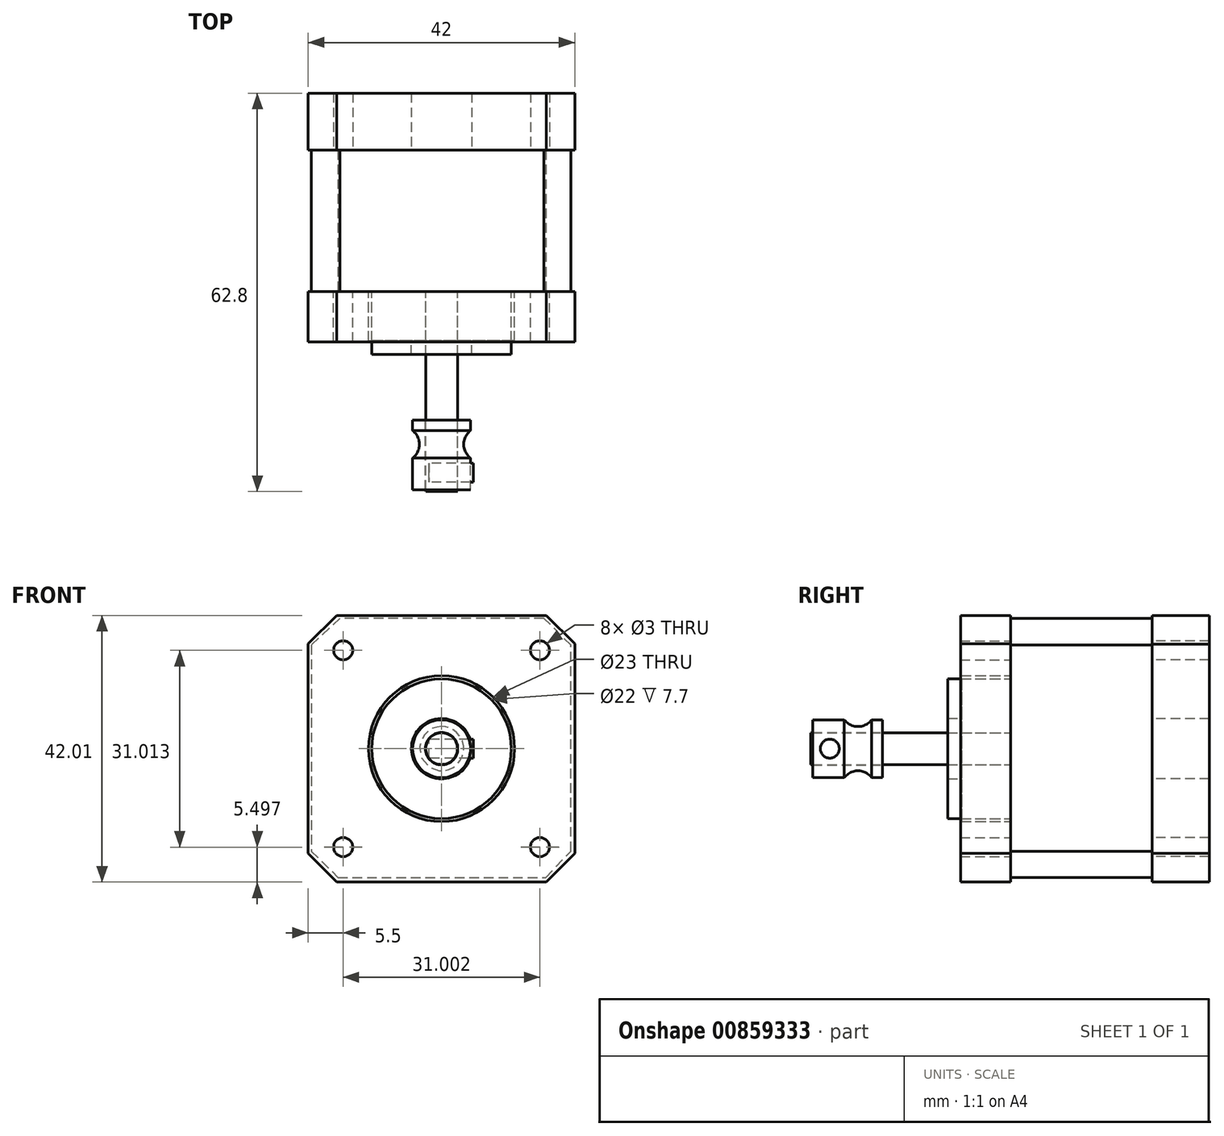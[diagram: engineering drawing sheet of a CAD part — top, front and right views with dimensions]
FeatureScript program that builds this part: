
annotation { "Feature Type Name" : "Feature", "Feature Type Description" : "" }
export const myFeature = defineFeature(function(context is Context, id is Id, definition is map)
    precondition{}
    {
        {
            var Q0;
            Q0=qCreatedBy(makeId("Front.planeOp"),FACE);
            var sketch = newSketch(context, id + "F0", { "sketchPlane" : qUnion([Q0])});
            skLineSegment(sketch, "E0.bottom", {"start": v(-16.5, 21) * mm, "end": v(16.5, 21) * mm});
            skLineSegment(sketch, "E0.top", {"start": v(-16.5, -21) * mm, "end": v(16.5, -21) * mm});
            skLineSegment(sketch, "E0.left", {"start": v(-21, 16.5) * mm, "end": v(-21, -16.5) * mm});
            skLineSegment(sketch, "E0.right", {"start": v(21, 16.5) * mm, "end": v(21, -16.5) * mm});
            skPoint(sketch, "E0.middle", {"position": v(0, 0) * mm});
            skLineSegment(sketch, "E1", {"start": v(-21, 16.5) * mm, "end": v(-16.5, 21) * mm});
            skLineSegment(sketch, "E2.MirrorCS", {"start": v(21, 16.5) * mm, "end": v(16.5, 21) * mm});
            skLineSegment(sketch, "E3.MirrorCS", {"start": v(-21, -16.5) * mm, "end": v(-16.5, -21) * mm});
            skLineSegment(sketch, "E4.MirrorCS", {"start": v(21, -16.5) * mm, "end": v(16.5, -21) * mm});
            skPoint(sketch, "E5.orphan", {"position": v(-21, 21) * mm});
            skPoint(sketch, "E6.orphan", {"position": v(-21, -21) * mm});
            skPoint(sketch, "E7.orphan", {"position": v(21, -21) * mm});
            skPoint(sketch, "E8.orphan", {"position": v(21, 21) * mm});
            skCircle(sketch, "E9", {"center": v(-15.5, 15.5) * mm, "radius": 1.5 * mm});
            skCircle(sketch, "E10.MirrorC", {"center": v(-15.5, -15.5) * mm, "radius": 1.5 * mm});
            skCircle(sketch, "E11.MirrorC", {"center": v(15.5, 15.5) * mm, "radius": 1.5 * mm});
            skCircle(sketch, "E12.MirrorC", {"center": v(15.5, -15.5) * mm, "radius": 1.5 * mm});
            skCircle(sketch, "E13", {"center": v(0, 0) * mm, "radius": 11 * mm});
            skCircle(sketch, "E14", {"center": v(0, 0) * mm, "radius": 2.5 * mm});
            skCircle(sketch, "E15", {"center": v(0, 0) * mm, "radius": 4.75 * mm});
            skCircle(sketch, "E16", {"center": v(0, 0) * mm, "radius": 11.5 * mm});
            skLineSegment(sketch, "E17", {"start": v(0, 0) * mm, "end": v(-109.37, 0) * mm, "construction": true});
            skSolve(sketch);
        }
        {
            var Q0;
            Q0=makeQuery(id+"F0.imprint","IMPRINT",FACE,{"disambiguationData":[TD([[makeQuery(id+"F0.imprint","IMPRINT",EDGE,{"derivedFrom":sQuery(id+"F0.wireOp",EDGE,"E0.bottom")}),-1.0]])]});
            extrude(context, id + "F1", {"entities" : qUnion([Q0]), "depth" : 7.9 * mm, "offsetDistance" : 25 * mm});
        }
        {
            var Q0;
            Q0=makeQuery(id+"F0.imprint","IMPRINT",FACE,{"disambiguationData":[TD([[makeQuery(id+"F0.imprint","IMPRINT",EDGE,{"derivedFrom":sQuery(id+"F0.wireOp",EDGE,"E13")}),1.0]])]});
            extrude(context, id + "F2", {"entities" : qUnion([Q0]), "operationType" : NewBodyOperationType.ADD, "depth" : 9.9 * mm, "offsetDistance" : 25 * mm});
        }
        {
            var Q0;
            Q0=makeQuery(id+"F0.imprint","IMPRINT",FACE,{"disambiguationData":[TD([[makeQuery(id+"F0.imprint","IMPRINT",EDGE,{"derivedFrom":sQuery(id+"F0.wireOp",EDGE,"E14")}),-1.0]])]});
            extrude(context, id + "F3", {"entities" : qUnion([Q0]), "operationType" : NewBodyOperationType.ADD, "depth" : 7.9 * mm, "offsetDistance" : 25 * mm});
        }
        {
            var Q0;
            Q0=makeQuery(id+"F0.imprint","IMPRINT",FACE,{"disambiguationData":[TD([[makeQuery(id+"F0.imprint","IMPRINT",EDGE,{"derivedFrom":sQuery(id+"F0.wireOp",EDGE,"E14")}),1.0]])]});
            var Q1;
            Q1=qSketchRegion(id+"F6",true);
            extrude(context, id + "F4", {"entities" : qUnion([Q0, Q1]), "depth" : 31.5 * mm, "offsetDistance" : 25 * mm});
        }
        {
            var Q0;
            Q0=makeQuery(id+"F0.imprint","IMPRINT",FACE,{"disambiguationData":[TD([[makeQuery(id+"F0.imprint","IMPRINT",EDGE,{"derivedFrom":sQuery(id+"F0.wireOp",EDGE,"E13")}),-1.0]])]});
            extrude(context, id + "F5", {"entities" : qUnion([Q0]), "depth" : 7.7 * mm, "offsetDistance" : 25 * mm});
        }
        {
            var Q0;
            Q0=qCreatedBy(makeId("Front.planeOp"),FACE);
            var sketch = newSketch(context, id + "F6", { "sketchPlane" : qUnion([Q0])});
            skLineSegment(sketch, "E18", {"start": v(16.13, 20.56) * mm, "end": v(-16.02, 20.56) * mm});
            skLineSegment(sketch, "E19", {"start": v(-16.02, 20.56) * mm, "end": v(-20.52, 16.32) * mm});
            skLineSegment(sketch, "E20", {"start": v(-20.52, 16.32) * mm, "end": v(-20.52, -16.15) * mm});
            skLineSegment(sketch, "E21", {"start": v(-20.52, -16.15) * mm, "end": v(-16.32, -20.27) * mm});
            skLineSegment(sketch, "E22", {"start": v(-16.32, -20.27) * mm, "end": v(16.41, -20.27) * mm});
            skLineSegment(sketch, "E23", {"start": v(16.41, -20.27) * mm, "end": v(20.38, -16.15) * mm});
            skLineSegment(sketch, "E24", {"start": v(20.38, -16.15) * mm, "end": v(20.38, 16.32) * mm});
            skLineSegment(sketch, "E25", {"start": v(20.38, 16.32) * mm, "end": v(16.13, 20.56) * mm});
            skSolve(sketch);
        }
        {
            var Q0;
            Q0=makeQuery(id+"F6.imprint","IMPRINT",FACE,{"disambiguationData":[TD([[makeQuery(id+"F6.imprint","IMPRINT",EDGE,{"derivedFrom":sQuery(id+"F6.wireOp",EDGE,"E18")}),1.0]])]});
            extrude(context, id + "F7", {"entities" : qUnion([Q0]), "depth" : -22.3 * mm, "offsetDistance" : 25 * mm});
        }
        {
            var Q0;
            Q0=makeQuery(id+"F7.opExtrude","CAP_FACE",FACE,{"disambiguationData":[OSD([sQuery(id+"F6.wireOp",EDGE,"E18"),sQuery(id+"F6.wireOp",EDGE,"E19"),sQuery(id+"F6.wireOp",EDGE,"E20"),sQuery(id+"F6.wireOp",EDGE,"E21"),sQuery(id+"F6.wireOp",EDGE,"E22"),sQuery(id+"F6.wireOp",EDGE,"E23"),sQuery(id+"F6.wireOp",EDGE,"E24"),sQuery(id+"F6.wireOp",EDGE,"E25")])],"isStart":false});
            var sketch = newSketch(context, id + "F8", { "sketchPlane" : qUnion([Q0])});
            skLineSegment(sketch, "E26.bottom", {"start": v(-16.5, 20.99) * mm, "end": v(16.5, 20.99) * mm});
            skLineSegment(sketch, "E26.top", {"start": v(-16.5, -21.01) * mm, "end": v(16.5, -21.01) * mm});
            skLineSegment(sketch, "E26.left", {"start": v(-21, 16.49) * mm, "end": v(-21, -16.51) * mm});
            skLineSegment(sketch, "E26.right", {"start": v(21, 16.49) * mm, "end": v(21, -16.51) * mm});
            skPoint(sketch, "E26.middle", {"position": v(0, -0.01) * mm});
            skLineSegment(sketch, "E27", {"start": v(-21, 16.49) * mm, "end": v(-16.5, 20.99) * mm});
            skLineSegment(sketch, "E28.MirrorCS", {"start": v(21, 16.49) * mm, "end": v(16.5, 20.99) * mm});
            skLineSegment(sketch, "E29.MirrorCS", {"start": v(-21, -16.51) * mm, "end": v(-16.5, -21.01) * mm});
            skLineSegment(sketch, "E30.MirrorCS", {"start": v(21, -16.51) * mm, "end": v(16.5, -21.01) * mm});
            skPoint(sketch, "E31.orphan", {"position": v(-21, 20.99) * mm});
            skPoint(sketch, "E32.orphan", {"position": v(-21, -21.01) * mm});
            skPoint(sketch, "E33.orphan", {"position": v(21, -21.01) * mm});
            skPoint(sketch, "E34.orphan", {"position": v(21, 20.99) * mm});
            skCircle(sketch, "E35", {"center": v(-15.5, 15.49) * mm, "radius": 1.5 * mm});
            skCircle(sketch, "E36.MirrorC", {"center": v(-15.5, -15.51) * mm, "radius": 1.5 * mm});
            skCircle(sketch, "E37.MirrorC", {"center": v(15.5, 15.49) * mm, "radius": 1.5 * mm});
            skCircle(sketch, "E38.MirrorC", {"center": v(15.5, -15.51) * mm, "radius": 1.5 * mm});
            skCircle(sketch, "E39", {"center": v(0, -0.01) * mm, "radius": 2.5 * mm});
            skCircle(sketch, "E40", {"center": v(0, -0.01) * mm, "radius": 4.75 * mm});
            skSolve(sketch);
        }
        {
            var Q0;
            Q0=qSketchRegion(id+"F8",true);
            extrude(context, id + "F9", {"entities" : qUnion([Q0]), "depth" : 9 * mm, "offsetDistance" : 25 * mm});
        }
        {
            var Q0;
            Q0=qCreatedBy(makeId("Right.planeOp"),FACE);
            var sketch = newSketch(context, id + "F10", { "sketchPlane" : qUnion([Q0])});
            skLineSegment(sketch, "E41", {"start": v(-31.2, 2.56) * mm, "end": v(-31.2, 4.56) * mm});
            skLineSegment(sketch, "E42", {"start": v(-31.2, 4.56) * mm, "end": v(-26.2, 4.56) * mm});
            skArc(sketch, "E43", {"start": v(-26.2, 4.56) * mm, "mid": v(-24.05, 3.48) * mm, "end": v(-21.9, 4.56) * mm});
            skLineSegment(sketch, "E44", {"start": v(-21.9, 4.56) * mm, "end": v(-20.2, 4.56) * mm});
            skLineSegment(sketch, "E45", {"start": v(-20.2, 4.56) * mm, "end": v(-20.2, 2.56) * mm});
            skLineSegment(sketch, "E46", {"start": v(-20.2, 2.56) * mm, "end": v(-31.2, 2.56) * mm});
            skLineSegment(sketch, "E47", {"start": v(0, 0) * mm, "end": v(-43.23, 0) * mm, "construction": true});
            skLineSegment(sketch, "E48", {"start": v(-24.05, 6.17) * mm, "end": v(-24.05, 14.68) * mm, "construction": true});
            skSolve(sketch);
        }
        {
            var Q0;
            Q0=makeQuery(id+"F10.imprint","IMPRINT",FACE,{"disambiguationData":[TD([[makeQuery(id+"F10.imprint","IMPRINT",EDGE,{"derivedFrom":sQuery(id+"F10.wireOp",EDGE,"E41")}),-1.0]])]});
            var Q1;
            Q1=sQuery(id+"F10.wireOp",EDGE,"E47");
            revolve(context, id + "F11", {"surfaceOperationType" : NewSurfaceOperationType.NEW, "entities" : qUnion([Q0]), "axis" : qUnion([Q1]), "revolveType" : RevolveType.FULL});
        }
        {
            var Q0;
            Q0=qCreatedBy(makeId("Right.planeOp"),FACE);
            var sketch = newSketch(context, id + "F12", { "sketchPlane" : qUnion([Q0])});
            skPoint(sketch, "E49", {"position": v(-28.5, 0) * mm});
            skCircle(sketch, "E50", {"center": v(-28.5, 0) * mm, "radius": 1.5 * mm});
            skSolve(sketch);
        }
        {
            var Q0;
            Q0=qSketchRegion(id+"F12",true);
            var Q1;
            Q1=sQuery(id+"F12.wireOp",EDGE,"E50");
            extrude(context, id + "F13", {"entities" : qUnion([Q0]), "surfaceEntities" : qUnion([Q1]), "depth" : 5 * mm, "offsetDistance" : 25 * mm, "hasSecondDirection" : true, "secondDirectionOppositeDirection" : true, "secondDirectionDepth" : 2 * mm});
        }
    });
